# Revit family: LeL Colorado 3.0
name_source: partatom
category: Lighting Fixtures
units: mm (PartAtom-declared; Revit-internal decimal feet)

## family parameters
Always vertical = No
Cut with Voids When Loaded = No
Light Source = No
OmniClass Number = 23.80.70.00
OmniClass Title = Lighting
Part Type = Normal
Room Calculation Point = No
Round Connector Dimension = Use Diameter
Shared = No
Work Plane-Based = Yes

## types (6) — shared parameters
Alimentazione = 230 V
Apparent Load = 41 VA
CCT = 3000 K
CRI = CRI80
Default Elevation = 1219 mm
Description = Outdoor/projectors
Finish = LeL Black
IK = IK09
IP = IP65 IP67 IP69
Lamp = LED
Manufacturer = L&L Luce&Light srl
Model = CA30
Rated Power supply = 230 V
URL = https://www.lucelight.it
Wattage = 41 W
Weight = 5.80 kg

## per-type parameters (varying)
| type | Lumen Output | Optic |
| 3.0 W 15°x50° 41W | 3461 lm | COLORADO Light source : 3.0 W 15°x50° 41W |
| 3.0 D 41W | 2255 lm | COLORADO Light source : 3.0 D 41W |
| 3.0 K 76° 41W | 3516 lm | COLORADO Light source : 3.0 K 76° 41W |
| 3.0 L 45° 41W | 3495 lm | COLORADO Light source : 3.0 L 45° 41W |
| 3.0 M 30° 41W | 3537 lm | COLORADO Light source : 3.0 M 30° 41W |
| 3.0 S 12° 41W | 3643 lm | COLORADO Light source : 3.0 S 12° 41W |

## geometry (parser evidence)
native form markers: Sweep x3
no freeform markers — native parametric forms only
